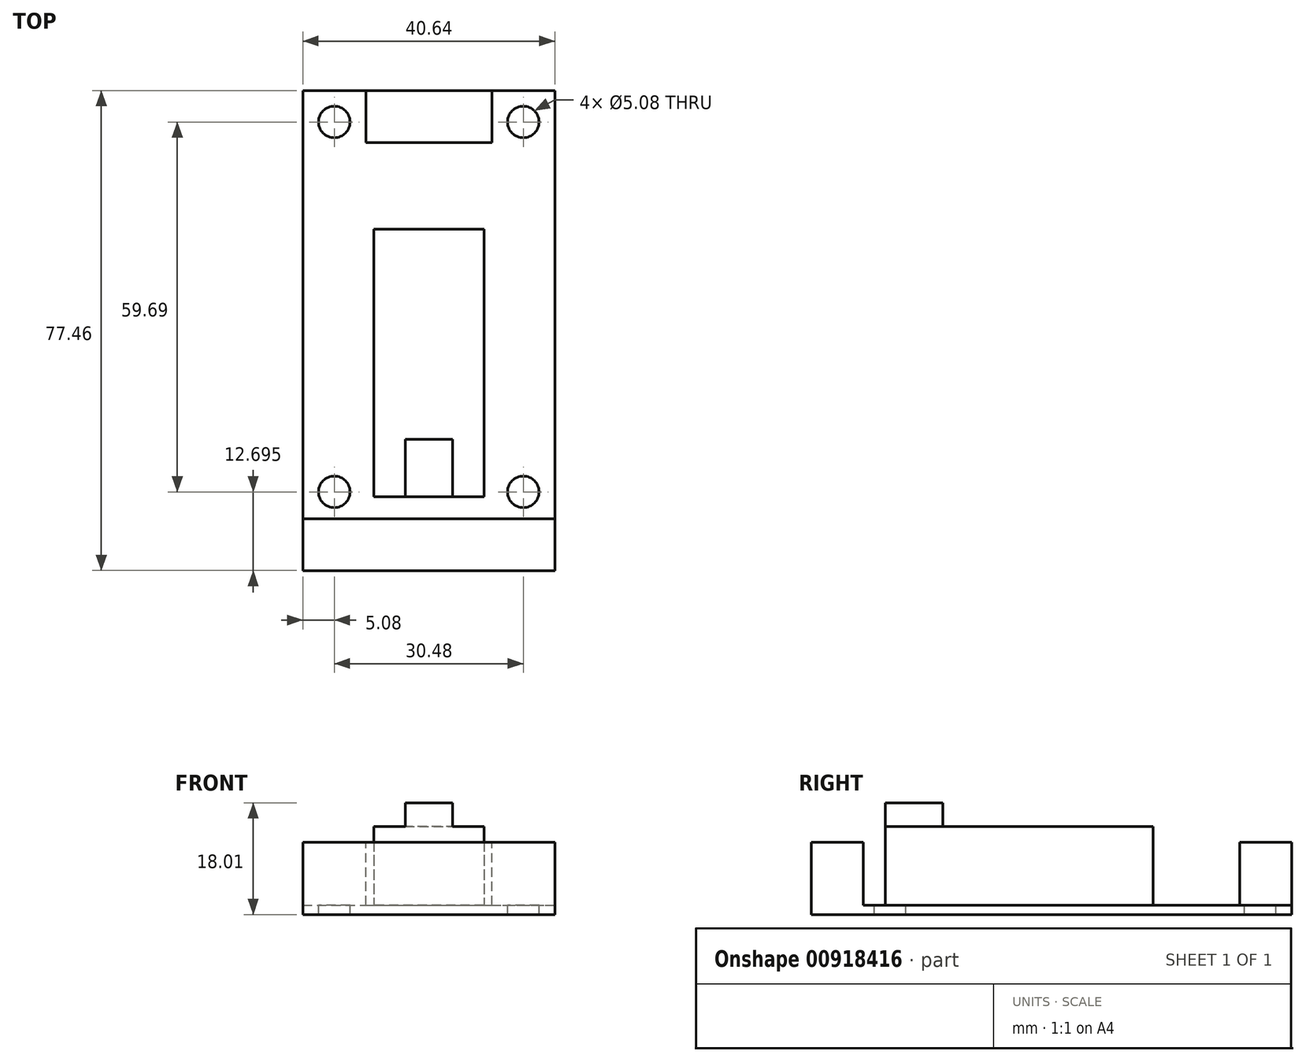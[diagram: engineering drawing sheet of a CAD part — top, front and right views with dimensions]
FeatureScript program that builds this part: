
annotation { "Feature Type Name" : "Feature", "Feature Type Description" : "" }
export const myFeature = defineFeature(function(context is Context, id is Id, definition is map)
    precondition{}
    {
        {
            var Q0;
            Q0=qCreatedBy(makeId("Top.planeOp"),FACE);
            var sketch = newSketch(context, id + "F0", { "sketchPlane" : qUnion([Q0])});
            skLineSegment(sketch, "E0.bottom", {"start": v(20.32, 38.73) * mm, "end": v(-20.32, 38.73) * mm});
            skLineSegment(sketch, "E0.top", {"start": v(20.32, -38.73) * mm, "end": v(-20.32, -38.73) * mm});
            skLineSegment(sketch, "E0.left", {"start": v(20.32, 38.73) * mm, "end": v(20.32, -38.73) * mm});
            skLineSegment(sketch, "E0.right", {"start": v(-20.32, 38.73) * mm, "end": v(-20.32, -38.73) * mm});
            skPoint(sketch, "E0.middle", {"position": v(0, 0) * mm});
            skSolve(sketch);
        }
        {
            var Q0;
            Q0 = qSketchRegion(id + "F0", true);
            extrude(context, id + "F1", {"entities" : qUnion([Q0]), "depth" : 1.5 * mm, "offsetDistance" : 25.4 * mm});
        }
        {
            var Q0;
            Q0=makeQuery(id+"F1.opExtrude","CAP_FACE",FACE,{"disambiguationData":[OSD([sQuery(id+"F0.wireOp",EDGE,"E0.bottom"),sQuery(id+"F0.wireOp",EDGE,"E0.top"),sQuery(id+"F0.wireOp",EDGE,"E0.left"),sQuery(id+"F0.wireOp",EDGE,"E0.right")])],"isStart":false});
            var sketch = newSketch(context, id + "F2", { "sketchPlane" : qUnion([Q0])});
            skLineSegment(sketch, "E1", {"start": v(-20.32, -38.73) * mm, "end": v(-20.32, -30.35) * mm});
            skLineSegment(sketch, "E2", {"start": v(-20.32, -30.35) * mm, "end": v(20.32, -30.35) * mm});
            skLineSegment(sketch, "E3", {"start": v(20.32, -38.73) * mm, "end": v(20.32, -30.35) * mm});
            skLineSegment(sketch, "E4", {"start": v(-20.32, 38.73) * mm, "end": v(-20.32, 30.35) * mm});
            skLineSegment(sketch, "E5", {"start": v(-20.32, 30.35) * mm, "end": v(20.32, 30.35) * mm});
            skSolve(sketch);
        }
        {
            var Q0;
            Q0 = qSketchRegion(id + "F2", true);
            var Q1;
            Q1=makeQuery(id+"F2.imprint","IMPRINT",FACE,{"disambiguationData":[TD([[makeQuery(id+"F2.imprint","IMPRINT",EDGE,{"derivedFrom":sQuery(id+"F2.wireOp",EDGE,"E4")}),1.0]])]});
            var Q2;
            Q2=makeQuery(id+"F2.imprint","IMPRINT",FACE,{"disambiguationData":[TD([[makeQuery(id+"F2.imprint","IMPRINT",EDGE,{"derivedFrom":sQuery(id+"F2.wireOp",EDGE,"E1")}),1.0]])]});
            extrude(context, id + "F3", {"entities" : qUnion([Q0, Q1, Q2]), "operationType" : NewBodyOperationType.ADD, "depth" : 10.16 * mm, "offsetDistance" : 25.4 * mm});
        }
        {
            var Q0;
            Q0=makeQuery(id+"F3.opExtrude","CAP_FACE",FACE,{"disambiguationData":[OSD([sQuery(id+"F0.wireOp",EDGE,"E0.bottom"),sQuery(id+"F0.wireOp",EDGE,"E0.left"),sQuery(id+"F2.wireOp",EDGE,"E4"),sQuery(id+"F2.wireOp",EDGE,"E5")])],"isStart":false});
            var sketch = newSketch(context, id + "F4", { "sketchPlane" : qUnion([Q0])});
            skLineSegment(sketch, "E6", {"start": v(-10.16, 30.35) * mm, "end": v(10.16, 30.35) * mm});
            skLineSegment(sketch, "E7", {"start": v(-10.16, 30.35) * mm, "end": v(-10.16, 38.73) * mm});
            skLineSegment(sketch, "E8", {"start": v(10.16, 30.35) * mm, "end": v(10.16, 38.73) * mm});
            skSolve(sketch);
        }
        {
            var Q0;
            Q0 = qSketchRegion(id + "F4", true);
            var Q1;
            {var subQ0=sQuery(id+"F4.wireOp",EDGE,"E7");Q1=makeQuery(id+"F4.imprint","IMPRINT",FACE,{"disambiguationData":[TD([[makeQuery(id+"F4.imprint","IMPRINT",EDGE,{"derivedFrom":subQ0}),1.0]])]});}
            var Q2;
            {var subQ0=sQuery(id+"F4.wireOp",EDGE,"E8");Q2=makeQuery(id+"F4.imprint","IMPRINT",FACE,{"disambiguationData":[TD([[makeQuery(id+"F4.imprint","IMPRINT",EDGE,{"derivedFrom":subQ0}),-1.0]])]});}
            var Q3;
            Q3=makeQuery(id+"F1.opExtrude","CAP_FACE",FACE,{"disambiguationData":[OSD([sQuery(id+"F0.wireOp",EDGE,"E0.bottom"),sQuery(id+"F0.wireOp",EDGE,"E0.top"),sQuery(id+"F0.wireOp",EDGE,"E0.left"),sQuery(id+"F0.wireOp",EDGE,"E0.right")])],"isStart":false});
            extrude(context, id + "F5", {"entities" : qUnion([Q0, Q1, Q2]), "operationType" : NewBodyOperationType.REMOVE, "endBound" : BoundingType.UP_TO_SURFACE, "oppositeDirection" : true, "depth" : 25.4 * mm, "endBoundEntityFace" : qUnion([Q3]), "offsetDistance" : 25.4 * mm});
        }
        {
            var Q0;
            Q0=makeQuery(id+"F1.opExtrude","CAP_FACE",FACE,{"disambiguationData":[OSD([sQuery(id+"F0.wireOp",EDGE,"E0.bottom"),sQuery(id+"F0.wireOp",EDGE,"E0.top"),sQuery(id+"F0.wireOp",EDGE,"E0.left"),sQuery(id+"F0.wireOp",EDGE,"E0.right")])],"isStart":false});
            var sketch = newSketch(context, id + "F6", { "sketchPlane" : qUnion([Q0])});
            skLineSegment(sketch, "E9.bottom", {"start": v(12.7, 33.65) * mm, "end": v(-12.7, 33.65) * mm});
            skLineSegment(sketch, "E9.top", {"start": v(12.7, -26.04) * mm, "end": v(-12.7, -26.04) * mm});
            skLineSegment(sketch, "E9.left", {"start": v(15.24, 31.11) * mm, "end": v(15.24, -23.5) * mm});
            skLineSegment(sketch, "E9.right", {"start": v(-15.24, 31.11) * mm, "end": v(-15.24, -23.5) * mm});
            skPoint(sketch, "E9.middle", {"position": v(0, 0) * mm});
            skLineSegment(sketch, "E10.bottom", {"start": v(-17.78, 33.65) * mm, "end": v(-20.32, 33.65) * mm});
            skLineSegment(sketch, "E10.top", {"start": v(-15.24, 38.73) * mm, "end": v(-20.32, 38.73) * mm});
            skLineSegment(sketch, "E10.left", {"start": v(-15.24, 36.2) * mm, "end": v(-15.24, 38.73) * mm});
            skLineSegment(sketch, "E10.right", {"start": v(-20.32, 33.65) * mm, "end": v(-20.32, 38.73) * mm});
            skPoint(sketch, "E10.middle", {"position": v(-17.78, 36.2) * mm});
            skLineSegment(sketch, "E11.bottom", {"start": v(20.32, 33.65) * mm, "end": v(17.78, 33.65) * mm});
            skLineSegment(sketch, "E11.top", {"start": v(20.32, 38.73) * mm, "end": v(15.24, 38.73) * mm});
            skLineSegment(sketch, "E11.left", {"start": v(20.32, 33.65) * mm, "end": v(20.32, 38.73) * mm});
            skLineSegment(sketch, "E11.right", {"start": v(15.24, 36.2) * mm, "end": v(15.24, 38.73) * mm});
            skPoint(sketch, "E11.middle", {"position": v(17.78, 36.2) * mm});
            skCircle(sketch, "E12", {"center": v(15.24, -26.04) * mm, "radius": 2.54 * mm});
            skCircle(sketch, "E13", {"center": v(15.24, 33.65) * mm, "radius": 2.54 * mm});
            skCircle(sketch, "E14", {"center": v(-15.24, 33.65) * mm, "radius": 2.54 * mm});
            skCircle(sketch, "E15", {"center": v(-15.24, -26.04) * mm, "radius": 2.54 * mm});
            skSolve(sketch);
        }
        {
            var Q0;
            {var subQ0=sQuery(id+"F6.wireOp",EDGE,"E14");var subQ1=makeQuery(id+"F6.imprint","INTERSECT",VERTEX,{"derivedFrom":[sQuery(id+"F6.wireOp",EDGE,"E9.bottom"),subQ0]});Q0=makeQuery(id+"F6.imprint","IMPRINT",FACE,{"disambiguationData":[TD([[makeQuery(id+"F6.imprint","IMPRINT",EDGE,{"disambiguationData":[TD([[subQ1,-1.0]])],"derivedFrom":subQ0}),1.0]])]});}
            var Q1;
            {var subQ0=sQuery(id+"F6.wireOp",EDGE,"E13");var subQ1=makeQuery(id+"F6.imprint","INTERSECT",VERTEX,{"derivedFrom":[sQuery(id+"F6.wireOp",EDGE,"E11.bottom"),subQ0]});Q1=makeQuery(id+"F6.imprint","IMPRINT",FACE,{"disambiguationData":[TD([[makeQuery(id+"F6.imprint","IMPRINT",EDGE,{"disambiguationData":[TD([[subQ1,-1.0]])],"derivedFrom":subQ0}),1.0]])]});}
            var Q2;
            {var subQ0=sQuery(id+"F6.wireOp",EDGE,"E12");var subQ1=makeQuery(id+"F6.imprint","INTERSECT",VERTEX,{"derivedFrom":[sQuery(id+"F6.wireOp",EDGE,"E9.top"),subQ0]});Q2=makeQuery(id+"F6.imprint","IMPRINT",FACE,{"disambiguationData":[TD([[makeQuery(id+"F6.imprint","IMPRINT",EDGE,{"disambiguationData":[TD([[subQ1,1.0]])],"derivedFrom":subQ0}),1.0]])]});}
            var Q3;
            {var subQ0=sQuery(id+"F6.wireOp",EDGE,"E15");var subQ1=makeQuery(id+"F6.imprint","INTERSECT",VERTEX,{"derivedFrom":[sQuery(id+"F6.wireOp",EDGE,"E9.top"),subQ0]});Q3=makeQuery(id+"F6.imprint","IMPRINT",FACE,{"disambiguationData":[TD([[makeQuery(id+"F6.imprint","IMPRINT",EDGE,{"disambiguationData":[TD([[subQ1,-1.0]])],"derivedFrom":subQ0}),1.0]])]});}
            var Q4;
            Q4=makeQuery(id+"F1.opExtrude","CAP_FACE",FACE,{"disambiguationData":[OSD([sQuery(id+"F0.wireOp",EDGE,"E0.bottom"),sQuery(id+"F0.wireOp",EDGE,"E0.top"),sQuery(id+"F0.wireOp",EDGE,"E0.left"),sQuery(id+"F0.wireOp",EDGE,"E0.right")])],"isStart":true});
            extrude(context, id + "F7", {"entities" : qUnion([Q0, Q1, Q2, Q3]), "operationType" : NewBodyOperationType.REMOVE, "endBound" : BoundingType.UP_TO_SURFACE, "oppositeDirection" : true, "depth" : 25.4 * mm, "endBoundEntityFace" : qUnion([Q4]), "offsetDistance" : 25.4 * mm});
        }
        {
            var Q0;
            {var subQ0=sQuery(id+"F2.wireOp",EDGE,"E5");var subQ1=sQuery(id+"F0.wireOp",EDGE,"E0.left");var subQ2=sQuery(id+"F0.wireOp",EDGE,"E0.bottom");Q0=makeQuery(id+"F5.boolean.opBoolean","MERGE",FACE,{"derivedFrom":[makeQuery(id+"F1.opExtrude","CAP_FACE",FACE,{"disambiguationData":[OSD([subQ2,sQuery(id+"F0.wireOp",EDGE,"E0.top"),subQ1,sQuery(id+"F0.wireOp",EDGE,"E0.right")])],"isStart":false})],"fromTools":[makeQuery(id+"F5.opExtrude","CAP_FACE",FACE,{"disambiguationData":[OSD([subQ2,sQuery(id+"F2.wireOp",EDGE,"E4"),subQ0,sQuery(id+"F4.wireOp",EDGE,"E7")])],"isStart":false}),makeQuery(id+"F5.opExtrude","CAP_FACE",FACE,{"disambiguationData":[OSD([subQ2,subQ1,subQ0,sQuery(id+"F4.wireOp",EDGE,"E8")])],"isStart":false})]});}
            var sketch = newSketch(context, id + "F8", { "sketchPlane" : qUnion([Q0])});
            skLineSegment(sketch, "E16.bottom", {"start": v(8.9, 16.38) * mm, "end": v(-8.89, 16.38) * mm});
            skLineSegment(sketch, "E16.top", {"start": v(8.9, -26.8) * mm, "end": v(-8.89, -26.8) * mm});
            skLineSegment(sketch, "E16.left", {"start": v(8.9, 16.38) * mm, "end": v(8.9, -26.8) * mm});
            skLineSegment(sketch, "E16.right", {"start": v(-8.89, 16.38) * mm, "end": v(-8.89, -26.8) * mm});
            skPoint(sketch, "E16.middle", {"position": v(0, -5.2) * mm});
            skLineSegment(sketch, "E17", {"start": v(0, 30.35) * mm, "end": v(0, 16.38) * mm});
            skSolve(sketch);
        }
        {
            var Q0;
            Q0 = qSketchRegion(id + "F8", true);
            extrude(context, id + "F9", {"entities" : qUnion([Q0]), "operationType" : NewBodyOperationType.ADD, "depth" : 12.7 * mm, "offsetDistance" : 25.4 * mm});
        }
        {
            var Q0;
            Q0=makeQuery(id+"F9.opExtrude","CAP_FACE",FACE,{"disambiguationData":[OSD([sQuery(id+"F8.wireOp",EDGE,"E16.bottom"),sQuery(id+"F8.wireOp",EDGE,"E16.top"),sQuery(id+"F8.wireOp",EDGE,"E16.left"),sQuery(id+"F8.wireOp",EDGE,"E16.right")])],"isStart":false});
            var sketch = newSketch(context, id + "F10", { "sketchPlane" : qUnion([Q0])});
            skLineSegment(sketch, "E18.bottom", {"start": v(-3.8, -26.8) * mm, "end": v(3.81, -26.8) * mm});
            skLineSegment(sketch, "E18.top", {"start": v(-3.8, -17.53) * mm, "end": v(3.81, -17.53) * mm});
            skLineSegment(sketch, "E18.left", {"start": v(-3.8, -26.8) * mm, "end": v(-3.8, -17.53) * mm});
            skLineSegment(sketch, "E18.right", {"start": v(3.81, -26.8) * mm, "end": v(3.81, -17.53) * mm});
            skPoint(sketch, "E18.middle", {"position": v(0, -22.16) * mm});
            skSolve(sketch);
        }
        {
            var Q0;
            Q0=makeQuery(id+"F10.imprint","IMPRINT",FACE,{"disambiguationData":[TD([[makeQuery(id+"F10.imprint","IMPRINT",EDGE,{"derivedFrom":sQuery(id+"F10.wireOp",EDGE,"E18.bottom")}),-1.0]])]});
            extrude(context, id + "F11", {"entities" : qUnion([Q0]), "operationType" : NewBodyOperationType.ADD, "depth" : 3.8 * mm, "offsetDistance" : 25.4 * mm});
        }
    });
